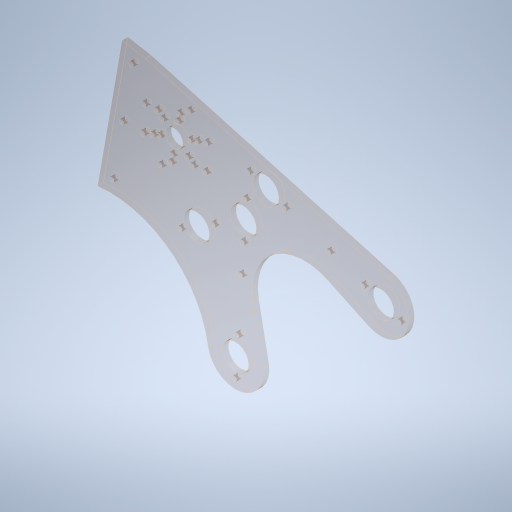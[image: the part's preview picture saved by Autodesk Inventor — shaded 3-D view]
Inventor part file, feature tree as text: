
AUTODESK INVENTOR PART (.ipt)
format: ipt  version: 2023.4 (Build 274418000, 418)  size: 428,544 bytes
history: native  units: in
note: dims shown in document units (in); Inventor stores cm internally (conversion verified against a paired STEP export)
features: sketch x2, hole x2, extrude x1, projected_geometry x1
ambient origin geometry x8: Origin, YZ Plane, XZ Plane, XY Plane, X Axis, Y Axis, Z Axis, Center Point
bodies: Solid1 (feature_tree)
feature tree (6):
  sketch  "Sketch1"  dims[d3=0.3489in d4=0.0in]
  extrude  "Extrusion1"  TaperAngle=0.0deg  [1 undecoded]
  hole  "Hole1"  [1 undecoded]
  hole  "Hole2"  [1 undecoded]
  sketch  "Sketch2"  dims[d7=4.0in d8=4.0in d9=1.123in d10=4.0in d11=4.5in d12=4.5in d13=0.625in d14=0.625in d15=5.2115in d16=1.125in d17=5.2115in d18=1.8765in d19=1.8765in d22=1.0in d23=6.0in d26=10.0585in d27=2.5in d30=8.0in d31=0.0687in d32=0.75in d33=4.75in d34=1.375in d35=0.75in d36=0.25in d38=2.3622in d40=360.0deg d44=0.375in d45=0.25in d46=0.0in d47=0.201in d48=0.75in d49=0.37in d50=0.25in d51=90.0deg d52=1.0in d53=0.8108in d55=0.5497in d56=0.3in d58=2.256in d59=2.5in d60=2.9555in d61=2.35in d62=0.3779in d65=2.0in d66=2.3622in d68=360.0deg d70=1.625in d71=60.0deg d72=1.655in d73=0.201in d74=0.75in d75=0.385in d76=0.25in d77=0.5635in d78=1.0in d79=0.8108in d80=1.5748in d82=360.0deg d85=1.5748in d87=360.0deg d89=45.0deg d90=0.25in d91=0.825in d92=4.25in]
  projected_geometry  "Projected Loop1"
note: 3 required parameter values undecoded (feature->parameter linkage not recoverable at this tier; creation-order binding heuristic only, values carry confidence <= 0.55)
